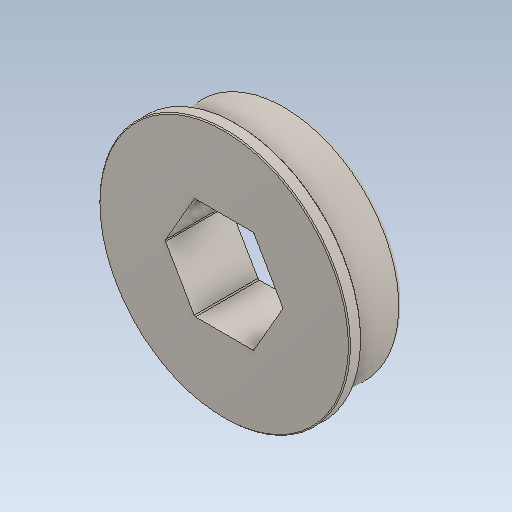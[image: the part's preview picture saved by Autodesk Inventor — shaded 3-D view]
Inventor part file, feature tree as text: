
AUTODESK INVENTOR PART (.ipt)
format: ipt  version: 2020 (Build 240168000, 168)  size: 162,304 bytes
history: native  units: in
note: dims shown in document units (in); Inventor stores cm internally (conversion verified against a paired STEP export)
features: fillet x1
ambient origin geometry x8: Origin, YZ Plane, XZ Plane, XY Plane, X Axis, Y Axis, Z Axis, Center Point
bodies: Solid1 (feature_tree)
feature tree (1):
  fillet  "Fillet2"  [1 undecoded]
note: 1 required parameter value undecoded (feature->parameter linkage not recoverable at this tier; creation-order binding heuristic only, values carry confidence <= 0.55)
